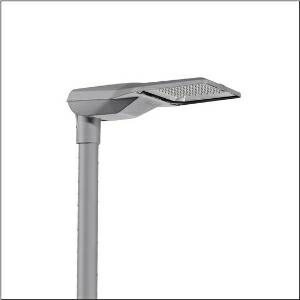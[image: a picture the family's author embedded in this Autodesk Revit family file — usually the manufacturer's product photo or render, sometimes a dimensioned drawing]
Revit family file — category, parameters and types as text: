
# Revit family: streetlight_sl_21_iq_midi___p0_8ab_5xe3r31d08mb_e13a
name_source: partatom
category: Lighting Fixtures
units: mm (PartAtom-declared; Revit-internal decimal feet)

## family parameters
Cut with Voids When Loaded = No
Host = Face
Light Source = No
Part Type = Normal
Room Calculation Point = No
Round Connector Dimension = Use Diameter
Shared = No

## types (1)
- --- (1 x LED, 16930 lm, 146.7 W, 3000K)
    Apparent Load = 147 VA
    CIE Flux Codes = 36 71 98 100 100
    Color Rendering = 70
    Color Temperature = 3000K
    Default Elevation = 1800 mm
    Description = Streetlight SL 21 iQ midi, mast luminaire, primary light control with lens, of PMMA, primary optical cover: cover, of toughened safety glass, transparent, light distribution: P0.8aB, light emission: direct distribution, primary light characteristic: asymmetric, installation type: post-top, side-entry, LED, High Power LED, rated luminous flux: 16.930lm, luminous efficacy: 115lm/W, light colour: 730, colour temperature: 3000K, control gear: iQ-Comfort, control: pre-setting: linear dimming characteristic, Auto-Match, Temp-Guard, Lumen-Switch, Night-Set, Smart-Wire, Light-Fading, Desk-Remote (wireless, voltage-free reading and setting of iQ features in the workshop via application-optimized NFC function/RFID function), optimised constant luminous flux control (CLO 2.0), mains connection: 230..240V, AC, 50/60Hz, start of lifetime: 147W, end of service life: 161W, reduction: 62W, luminaire housing, of diecast aluminium, powder-coated, SITECO metallic grey (DB 702S), corrosivity category C5 high according to DIN EN ISO 12944, please order mast flange separately, inclination adjustable: 0°, 5°, 10°, 15°, sealing non-destructively replaceable, multi-level sealing system, length: 644mm, width: 335mm, height: 110mm, mast flange for spigot size: 42mm (side-entry): 5XC10008XM4, 60/48mm (side-entry/post-top): 5XC10108XM2, 76/60mm (side-entry/post-top): 5XC10108XM1, mounting height: 4..8m, protection rating (complete): IP66, insulation class (complete): insulation class II (safety insulation), certification: CE, ENEC, ENEC+, VDE, impact resistance: IK10, permissible operating ambient temperature for outdoor applications: -40..+50°C, standard-compliant lighting for roads and squares, packaging unit: 1 piece

Light Distribution: P0.8aB
    Height = 111 mm
    Lamp = 1 x LED
    Lamp Light Flux = 16930 lm
    Lamp Power = 146.7 W
    Lamp count = 1
    Length = 644 mm
    Luminous efficacy = 115 lm/W
    Manufacturer = Siteco
    ModVariant = No
    Model = 5XE3R31D08MB
    Number of Poles = 1
    OnlyDefault = Yes
    Power Factor = 1
    Product Name = Streetlight SL 21 iQ midi | P0.8aB
    Product group = mast luminaire | pylon top
    ProductGroupID = 6100
    Protection Class = Protection class II
    Protection Degree = IP 66
    RLX_Detail_Level = 1
    RLX_Emergency_Light_Flux = 0 lm
    RLX_Emergency_Type = 0
    RLX_Emergency_Type_DB = No
    RlxData = <blob elided: 91597 chars, md5=89b874d4>
    Socket = socket
    Standby Power = 0 W
    System Light Flux = 16931 lm
    System Power = 147 W
    Type Comments = factory setting: luminous flux: 100 % | dim-lin: 254 | 753 mA
    Type Image = l_1004298.jpg
    URL = http://relux.com
    VarID = @adj_082149
    Voltage = 0 V
    Weight = 0.00 kg
    Width = 336 mm

## geometry (parser evidence)
native form markers: Blend x4, Sweep x9
no freeform markers — native parametric forms only
